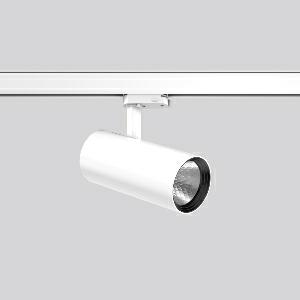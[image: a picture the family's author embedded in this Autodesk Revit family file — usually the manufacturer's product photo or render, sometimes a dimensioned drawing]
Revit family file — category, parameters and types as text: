
# Revit family: deecos_s_mini_742204_002_3_bc00
name_source: partatom
category: Lighting Fixtures
units: mm (PartAtom-declared; Revit-internal decimal feet)

## family parameters
Cut with Voids When Loaded = No
Host = Face
Light Source = No
Part Type = Normal
Room Calculation Point = No
Round Connector Dimension = Use Diameter
Shared = No

## types (1)
- DEECOS S mini (1 x LED Modul 935, 3600 lm, 3500)
    Apparent Load = 29 VA
    Approval mark = CE
    CIE Flux Codes = 99 100 100 100 100
    Color Rendering = 92
    Color Temperature = 3500
    Default Elevation = 1800 mm
    Description = Series: DEECOS S mini
LED surface-mounted projector in modern design with no visible cooling ribs. Housing: die-cast aluminium, powder-coated. Rotation range: 356°. Swivel range: 90°. Black plastic ring and recessed LED to prevent glare from the side. Optical assembly with reflector made of MIRO-Silver with 98% total light reflection for outstanding efficiency - can be changed without tools. Best colour rendering index Ra>90. With multi adaptor for 3-circuit tracks 230 V. Suitable for Track on ceiling, Wall track. High quality converter without flickering and stroboscopic effect. The following accessories can be mounted without use of tools: interchangeable lenses, decorative glasses, honeycomb louvre, clear and frosted diffusers, white interchangeable plastic ring. 
Colour: traffic white, matt (RAL 9016)
Diameter: 87 mm
Height: 214 mm
Lamp: LED
Socket: without socket
Colour temperature: 3500K
Colour rendering index (CRI): 92
System power: 29 W
Rated luminous flux: 3600 lm
Luminous efficiency: 124 lm/W
Control gear: Regulated power supply
Protection class: I
Type of protection: IP 20
    Height = 214 mm
    Lamp = 1 x LED Modul 935
    Lamp Light Flux = 3600 lm
    Lamp count = 1
    Length = 87 mm
    Lifetime = 50000 h
    Luminous efficacy = 124 lm/W
    Manufacturer = RZB
    ModVariant = No
    Model = 742204.002.3
    Mounting Place = Ceiling
    Mounting Type = Rail mounted
    Number of Poles = 1
    OnlyDefault = Yes
    Power Factor = 1
    Product Name = DEECOS S mini
    Product group = Track mounted projectors
    ProductGroupID = 301
    Protection Class = Protection class I
    Protection Degree = IP 20
    RLX_Detail_Level = 1
    RLX_Emergency_Light_Flux = 0 lm
    RLX_Emergency_Type = 0
    RLX_Emergency_Type_DB = No
    RlxData = <blob elided: 35289 chars, md5=68a81ee8>
    Socket = socket
    Standby Power = 0 W
    System Light Flux = 3600 lm
    System Power = 29 W
    Type Comments = Product without accessories
    Type Image = 741926.002.jpg
    URL = http://relux.com
    VarID = ---
    Voltage = 230 V
    Voltage Range = 220-240 V
    Weight = 0.00 kg
    Width = 0 mm  [stored 0 ft]

note: [stored X ft] marks values corroborated as IEEE doubles in the binary element streams (Revit-internal decimal feet)

## geometry (parser evidence)
native form markers: Blend x4, Sweep x11
no freeform markers — native parametric forms only
